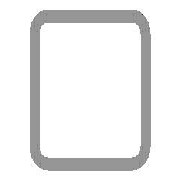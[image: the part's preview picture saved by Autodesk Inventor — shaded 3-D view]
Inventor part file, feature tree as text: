
AUTODESK INVENTOR PART (.ipt)
format: ipt  version: 2018 (Build 220112000, 112)  size: 161,792 bytes
history: native  units: mm (DEFAULTED — no unit token found)
features: other x6, sketch x5, extrude x2, hole x1, plane x1, reference x1
ambient origin geometry x8: Origin, YZ Plane, XZ Plane, XY Plane, X Axis, Y Axis, Z Axis, Center Point
bodies: Solid1 (feature_tree)
feature tree (16):
  other  "Driven Length"
  other  "Piano iniziale"
  other  "Piano finale"
  extrude  "Corpo"  TaperAngle=0.0deg  [1 undecoded]
  extrude  "Estrusione2"  Depth=40.0mm
  hole  "Foro1"  [1 undecoded]
  sketch  "Schizzo"
  sketch  "Sketch3"  dims[d3=700.0mm d4=0.0mm]
  plane  "Work Plane3"
  sketch  "Sketch4"  dims[d7=4.0mm d9=40.0mm d11=40.0mm d12=2.0mm d13=-0.0mm d14=700.0mm d15=20.0mm d16=20.0mm d17=90.0deg d18=700.0mm d19=45.0deg d20=45.0deg d21=10.0mm d22=0.0mm d23=10.0mm d24=6.0mm d25=4.0mm d26=2.0mm d27=90.0deg d28=8.0mm d29=20.594885mm]
  sketch  "Schizzo5"
  sketch  "Schizzo6"
  reference  "Riferimento1"
  other  "<userpath>\no-brim\Meccanica\Progetto Inventor no-brim\Assiemi\Telaio - Trasporto.iam"
  other  "Telaio - Trasporto.iam"
  other  "Tubolari horizontal:1"
note: 2 required parameter values undecoded (feature->parameter linkage not recoverable at this tier; creation-order binding heuristic only, values carry confidence <= 0.55)
